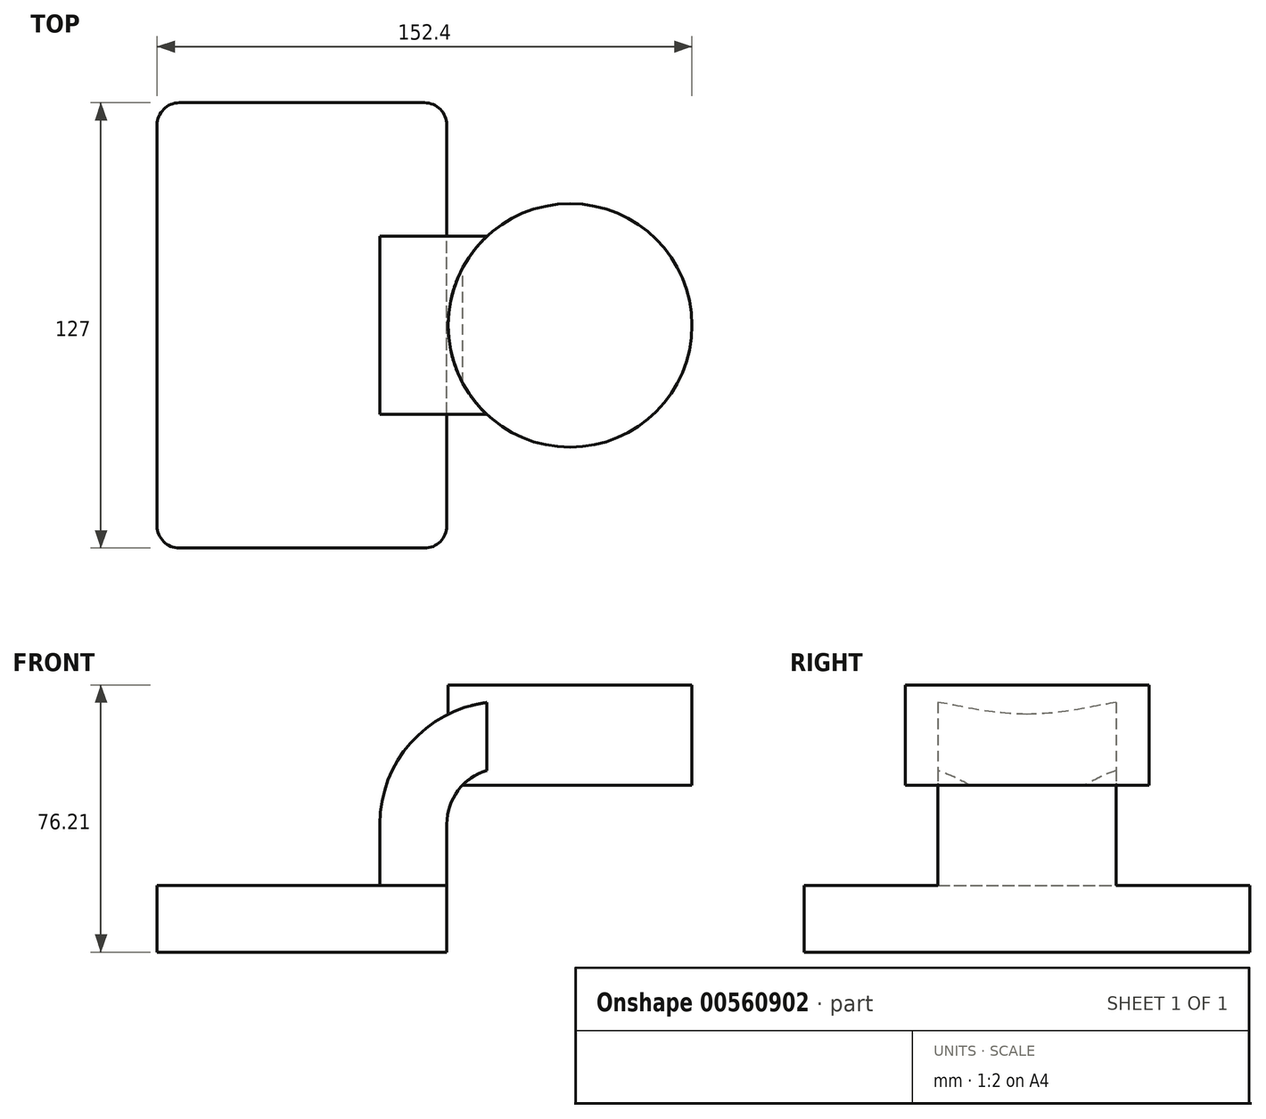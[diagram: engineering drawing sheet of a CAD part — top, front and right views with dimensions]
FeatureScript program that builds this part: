
annotation { "Feature Type Name" : "Feature", "Feature Type Description" : "" }
export const myFeature = defineFeature(function(context is Context, id is Id, definition is map)
    precondition{}
    {
        {
            var Q0;
            Q0=qCreatedBy(makeId("Front.planeOp"),FACE);
            var sketch = newSketch(context, id + "F0", { "sketchPlane" : qUnion([Q0])});
            skLineSegment(sketch, "E0.bottom", {"start": v(41.27, 9.52) * mm, "end": v(-41.28, 9.52) * mm});
            skLineSegment(sketch, "E0.top", {"start": v(41.27, -9.53) * mm, "end": v(-41.27, -9.53) * mm});
            skLineSegment(sketch, "E0.left", {"start": v(41.28, 9.52) * mm, "end": v(41.28, -9.53) * mm});
            skLineSegment(sketch, "E0.right", {"start": v(-41.27, 9.52) * mm, "end": v(-41.27, -9.53) * mm});
            skPoint(sketch, "E0.middle", {"position": v(0, 0) * mm});
            skLineSegment(sketch, "E1.bottom", {"start": v(60.32, 66.67) * mm, "end": v(111.12, 66.67) * mm});
            skLineSegment(sketch, "E1.top", {"start": v(60.33, 38.1) * mm, "end": v(111.13, 38.1) * mm});
            skLineSegment(sketch, "E1.left", {"start": v(60.32, 66.67) * mm, "end": v(60.33, 38.1) * mm});
            skLineSegment(sketch, "E1.right", {"start": v(111.13, 66.67) * mm, "end": v(111.13, 38.1) * mm});
            skPoint(sketch, "E1.middle", {"position": v(85.73, 52.39) * mm});
            skLineSegment(sketch, "E2", {"start": v(41.27, 9.52) * mm, "end": v(41.27, 27) * mm});
            skArc(sketch, "E3", {"start": v(41.28, 27) * mm, "mid": v(45.92, 38.23) * mm, "end": v(57.15, 42.88) * mm});
            skLineSegment(sketch, "E4", {"start": v(57.15, 42.88) * mm, "end": v(76.4, 42.88) * mm});
            skArc(sketch, "E5.0", {"start": v(22.23, 27) * mm, "mid": v(32.45, 51.7) * mm, "end": v(57.15, 61.93) * mm});
            skLineSegment(sketch, "E6", {"start": v(22.23, 27) * mm, "end": v(22.23, 9.52) * mm});
            skLineSegment(sketch, "E7", {"start": v(57.15, 61.93) * mm, "end": v(76.4, 61.93) * mm});
            skLineSegment(sketch, "E8", {"start": v(76.4, 38.1) * mm, "end": v(76.4, 66.67) * mm});
            skFitSpline(sketch, "E9", {"points": [v(-41.28, 9.53) * mm, v(57.15, 61.93) * mm], "startDerivative": vector(28.34, 75.07) * mm, "endDerivative": vector(191.84, -1.03) * mm});
            skSolve(sketch);
        }
        {
            var Q0;
            Q0=makeQuery(id+"F0.imprint","IMPRINT",FACE,{"disambiguationData":[TD([[makeQuery(id+"F0.imprint","IMPRINT",EDGE,{"derivedFrom":sQuery(id+"F0.wireOp",EDGE,"E0.top")}),-1.0]])]});
            extrude(context, id + "F1", {"entities" : qUnion([Q0]), "endBound" : BoundingType.SYMMETRIC, "depth" : 127 * mm, "offsetDistance" : 25.4 * mm});
        }
        {
            var Q0;
            {var subQ1=sQuery(id+"F0.wireOp",EDGE,"E2");Q0=makeQuery(id+"F0.imprint","IMPRINT",FACE,{"disambiguationData":[TD([[makeQuery(id+"F0.imprint","IMPRINT",EDGE,{"derivedFrom":subQ1}),1.0]])]});}
            var Q1;
            {var subQ0=sQuery(id+"F0.wireOp",EDGE,"E7");var subQ1=sQuery(id+"F0.wireOp",EDGE,"E1.left");var subQ2=makeQuery(id+"F0.imprint","INTERSECT",VERTEX,{"derivedFrom":[subQ1,subQ0]});Q1=makeQuery(id+"F0.imprint","IMPRINT",FACE,{"disambiguationData":[TD([[makeQuery(id+"F0.imprint","IMPRINT",EDGE,{"disambiguationData":[TD([[subQ2,-1.0]])],"derivedFrom":subQ1}),1.0]])]});}
            extrude(context, id + "F2", {"entities" : qUnion([Q0, Q1]), "operationType" : NewBodyOperationType.ADD, "endBound" : BoundingType.SYMMETRIC, "depth" : 50.8 * mm, "offsetDistance" : 25.4 * mm});
        }
        {
            var Q0;
            Q0=makeQuery(id+"F0.imprint","IMPRINT",FACE,{"disambiguationData":[TD([[makeQuery(id+"F0.imprint","IMPRINT",EDGE,{"derivedFrom":sQuery(id+"F0.wireOp",EDGE,"E5.0")}),1.0]])]});
            extrude(context, id + "F3", {"entities" : qUnion([Q0]), "operationType" : NewBodyOperationType.ADD, "endBound" : BoundingType.SYMMETRIC, "depth" : 15.88 * mm, "offsetDistance" : 25.4 * mm});
        }
        {
            var Q0;
            {var subQ0=sQuery(id+"F0.wireOp",EDGE,"E1.right");Q0=makeQuery(id+"F0.imprint","IMPRINT",FACE,{"disambiguationData":[TD([[makeQuery(id+"F0.imprint","IMPRINT",EDGE,{"derivedFrom":subQ0}),-1.0]])]});}
            var Q1;
            Q1=sQuery(id+"F0.wireOp",EDGE,"E8");
            revolve(context, id + "F4", {"operationType" : NewBodyOperationType.ADD, "entities" : qUnion([Q0]), "axis" : qUnion([Q1]), "revolveType" : RevolveType.FULL});
        }
        {
            var Q0;
            Q0=makeQuery(id+"F1.opExtrude","CAP_EDGE",EDGE,{"disambiguationData":[OSD([sQuery(id+"F0.wireOp",EDGE,"E0.right")])],"isStart":false});
            var Q1;
            Q1=makeQuery(id+"F1.opExtrude","CAP_EDGE",EDGE,{"disambiguationData":[OSD([sQuery(id+"F0.wireOp",EDGE,"E0.left")])],"isStart":false});
            var Q2;
            Q2=makeQuery(id+"F1.opExtrude","CAP_EDGE",EDGE,{"disambiguationData":[OSD([sQuery(id+"F0.wireOp",EDGE,"E0.left")])],"isStart":true});
            var Q3;
            Q3=makeQuery(id+"F1.opExtrude","CAP_EDGE",EDGE,{"disambiguationData":[OSD([sQuery(id+"F0.wireOp",EDGE,"E0.right")])],"isStart":true});
            fillet(context, id + "F5", {"entities" : qUnion([Q0, Q1, Q2, Q3]), "radius" : 6.35 * mm, "tangentPropagation" : true, "allowEdgeOverflow" : false});
        }
    });
